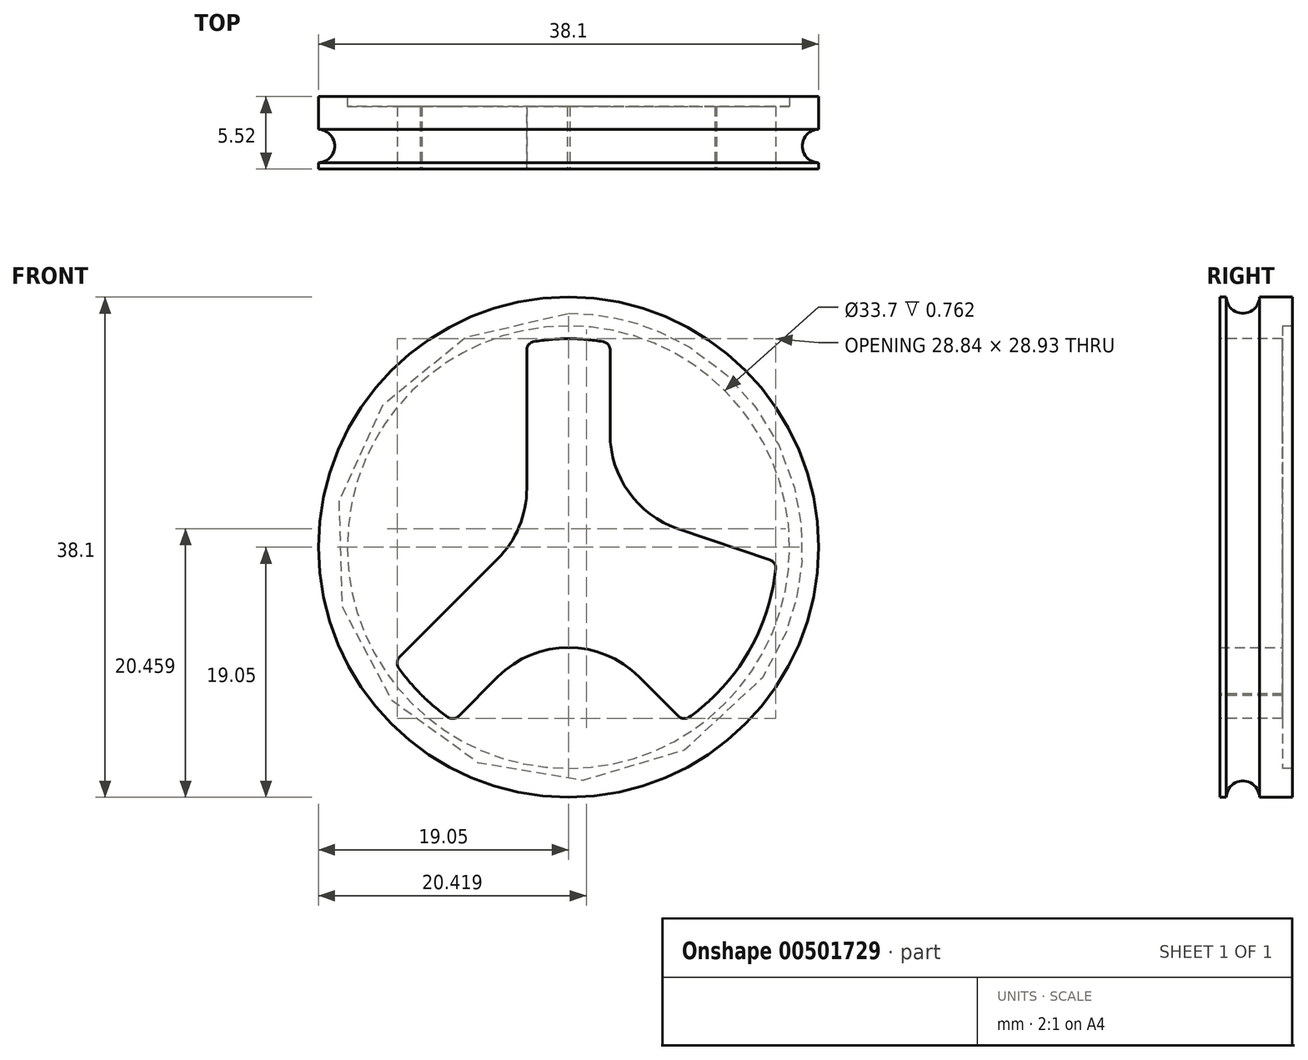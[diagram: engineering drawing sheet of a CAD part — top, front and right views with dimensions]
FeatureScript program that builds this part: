
annotation { "Feature Type Name" : "Feature", "Feature Type Description" : "" }
export const myFeature = defineFeature(function(context is Context, id is Id, definition is map)
    precondition{}
    {
        {
            var Q0;
            Q0=qCreatedBy(makeId("Front.planeOp"),FACE);
            var sketch = newSketch(context, id + "F0", { "sketchPlane" : qUnion([Q0])});
            skCircle(sketch, "E0", {"center": v(0, 0) * mm, "radius": 19.05 * mm});
            skSolve(sketch);
        }
        {
            var Q0;
            Q0=qSketchRegion(id+"F0",true);
            extrude(context, id + "F1", {"entities" : qUnion([Q0]), "depth" : 4.76 * mm});
        }
        {
            var Q0;
            Q0=makeQuery(id+"F1.opExtrude","CAP_FACE",FACE,{"disambiguationData":[OSD([sQuery(id+"F0.wireOp",EDGE,"E0")])],"isStart":false});
            var sketch = newSketch(context, id + "F2", { "sketchPlane" : qUnion([Q0])});
            skArc(sketch, "E1.3.0", {"start": v(-11.29, -11.16) * mm, "mid": v(-11.22, -11.23) * mm, "end": v(-11.16, -11.3) * mm});
            skArc(sketch, "E1.5.0", {"start": v(11.16, -11.29) * mm, "mid": v(11.23, -11.23) * mm, "end": v(11.3, -11.16) * mm});
            skPoint(sketch, "E1.center", {"position": v(0, 0) * mm});
            skLineSegment(sketch, "E2", {"start": v(-2.24, 2.24) * mm, "end": v(-13.32, -8.83) * mm});
            skLineSegment(sketch, "E3", {"start": v(-3.17, 0) * mm, "end": v(-3.18, 15.55) * mm});
            skLineSegment(sketch, "E4", {"start": v(3.18, 3.17) * mm, "end": v(3.17, 15.55) * mm});
            skLineSegment(sketch, "E5", {"start": v(3.17, 15.42) * mm, "end": v(3.1, 15.09) * mm});
            skArc(sketch, "E6", {"start": v(-13.24, -8.76) * mm, "mid": v(-11.22, -11.23) * mm, "end": v(-8.75, -13.25) * mm});
            skArc(sketch, "E7.trimOffspring", {"start": v(0.1, 15.87) * mm, "mid": v(0, 15.87) * mm, "end": v(-0.1, 15.87) * mm});
            skArc(sketch, "E8.trimOffspring", {"start": v(3.17, 15.55) * mm, "mid": v(0, 15.87) * mm, "end": v(-3.18, 15.55) * mm});
            skArc(sketch, "E9.trimOffspring", {"start": v(8.76, -13.24) * mm, "mid": v(14.67, -6.08) * mm, "end": v(15.55, 3.18) * mm});
            skLineSegment(sketch, "E10.trimOffspring", {"start": v(0, -4.5) * mm, "end": v(8.76, -13.24) * mm});
            skLineSegment(sketch, "E11.trimOffspring", {"start": v(0, -4.5) * mm, "end": v(-8.75, -13.25) * mm});
            skArc(sketch, "E12.trimOffspring", {"start": v(-2.24, 2.24) * mm, "mid": v(-2.93, 1.21) * mm, "end": v(-3.17, 0) * mm});
            skPoint(sketch, "E13.end.orphan", {"position": v(3.18, 0) * mm});
            skLineSegment(sketch, "E14", {"start": v(3.18, 3.17) * mm, "end": v(15.83, -1.15) * mm});
            skSolve(sketch);
        }
        {
            var Q0;
            Q0 = qSketchRegion(id + "F2", true);
            extrude(context, id + "F3", {"entities" : qUnion([Q0]), "operationType" : NewBodyOperationType.REMOVE, "oppositeDirection" : true, "depth" : 25.4 * mm});
        }
        {
            var Q0;
            Q0=makeQuery(id+"F3.boolean.opBoolean","COPY",EDGE,{"derivedFrom":makeQuery(id+"F3.opExtrude","SWEPT_EDGE",EDGE,{"disambiguationData":[OSD([sQuery(id+"F2.wireOp",EDGE,"E2"),sQuery(id+"F2.wireOp",EDGE,"E6")])]})});
            var Q1;
            Q1=makeQuery(id+"F3.boolean.opBoolean","COPY",EDGE,{"derivedFrom":makeQuery(id+"F3.opExtrude","SWEPT_EDGE",EDGE,{"disambiguationData":[OSD([sQuery(id+"F2.wireOp",EDGE,"E6"),sQuery(id+"F2.wireOp",EDGE,"E11.trimOffspring")])]})});
            var Q2;
            Q2=makeQuery(id+"F3.boolean.opBoolean","COPY",EDGE,{"derivedFrom":makeQuery(id+"F3.opExtrude","SWEPT_EDGE",EDGE,{"disambiguationData":[OSD([sQuery(id+"F2.wireOp",EDGE,"E9.trimOffspring"),sQuery(id+"F2.wireOp",EDGE,"E10.trimOffspring")])]})});
            var Q3;
            Q3=makeQuery(id+"F3.boolean.opBoolean","COPY",EDGE,{"derivedFrom":makeQuery(id+"F3.opExtrude","SWEPT_EDGE",EDGE,{"disambiguationData":[OSD([sQuery(id+"F2.wireOp",EDGE,"E9.trimOffspring"),sQuery(id+"F2.wireOp",EDGE,"E14")])]})});
            var Q4;
            Q4=makeQuery(id+"F3.boolean.opBoolean","COPY",EDGE,{"derivedFrom":makeQuery(id+"F3.opExtrude","SWEPT_EDGE",EDGE,{"disambiguationData":[OSD([sQuery(id+"F2.wireOp",EDGE,"E4"),sQuery(id+"F2.wireOp",EDGE,"E8.trimOffspring")])]})});
            var Q5;
            Q5=makeQuery(id+"F3.boolean.opBoolean","COPY",EDGE,{"derivedFrom":makeQuery(id+"F3.opExtrude","SWEPT_EDGE",EDGE,{"disambiguationData":[OSD([sQuery(id+"F2.wireOp",EDGE,"E3"),sQuery(id+"F2.wireOp",EDGE,"E8.trimOffspring")])]})});
            fillet(context, id + "F4", {"entities" : qUnion([Q0, Q1, Q2, Q3, Q4, Q5]), "radius" : 0.64 * mm, "tangentPropagation" : true, "allowEdgeOverflow" : false});
        }
        {
            var Q0;
            Q0=makeQuery(id+"F3.boolean.opBoolean","COPY",EDGE,{"derivedFrom":makeQuery(id+"F3.opExtrude","SWEPT_EDGE",EDGE,{"disambiguationData":[OSD([sQuery(id+"F2.wireOp",EDGE,"E2"),sQuery(id+"F2.wireOp",EDGE,"E3")])]})});
            var Q1;
            Q1=makeQuery(id+"F3.boolean.opBoolean","COPY",EDGE,{"derivedFrom":makeQuery(id+"F3.opExtrude","SWEPT_EDGE",EDGE,{"disambiguationData":[OSD([sQuery(id+"F2.wireOp",EDGE,"E10.trimOffspring"),sQuery(id+"F2.wireOp",EDGE,"E11.trimOffspring")])]})});
            var Q2;
            Q2=makeQuery(id+"F3.boolean.opBoolean","COPY",EDGE,{"derivedFrom":makeQuery(id+"F3.opExtrude","SWEPT_EDGE",EDGE,{"disambiguationData":[OSD([sQuery(id+"F2.wireOp",EDGE,"E4"),sQuery(id+"F2.wireOp",EDGE,"E14")])]})});
            fillet(context, id + "F5", {"entities" : qUnion([Q0, Q1, Q2]), "radius" : 7.62 * mm, "tangentPropagation" : true, "allowEdgeOverflow" : false});
        }
        {
            var Q0;
            Q0=makeQuery(id+"F1.opExtrude","CAP_FACE",FACE,{"disambiguationData":[OSD([sQuery(id+"F0.wireOp",EDGE,"E0")])],"isStart":true});
            var sketch = newSketch(context, id + "F6", { "sketchPlane" : qUnion([Q0])});
            skCircle(sketch, "E15", {"center": v(0, 0) * mm, "radius": 19.05 * mm});
            skCircle(sketch, "E16", {"center": v(0, 0) * mm, "radius": 16.85 * mm});
            skSolve(sketch);
        }
        {
            var Q0;
            Q0 = qSketchRegion(id + "F6", true);
            extrude(context, id + "F7", {"entities" : qUnion([Q0]), "operationType" : NewBodyOperationType.ADD, "depth" : 0.76 * mm});
        }
        {
            var Q0;
            Q0=qCreatedBy(makeId("Top.planeOp"),FACE);
            var sketch = newSketch(context, id + "F8", { "sketchPlane" : qUnion([Q0])});
            skCircle(sketch, "E17", {"center": v(-19.08, -3) * mm, "radius": 1.27 * mm});
            skSolve(sketch);
        }
        {
            var Q0;
            Q0 = qSketchRegion(id + "F8", true);
            var Q1;
            Q1=makeQuery(id+"F7.opExtrude","CAP_EDGE",EDGE,{"disambiguationData":[OSD([sQuery(id+"F6.wireOp",EDGE,"E16")])],"isStart":false});
            revolve(context, id + "F9", {"operationType" : NewBodyOperationType.REMOVE, "entities" : qUnion([Q0]), "axis" : qUnion([Q1]), "revolveType" : RevolveType.FULL, "oppositeDirection" : true});
        }
    });
